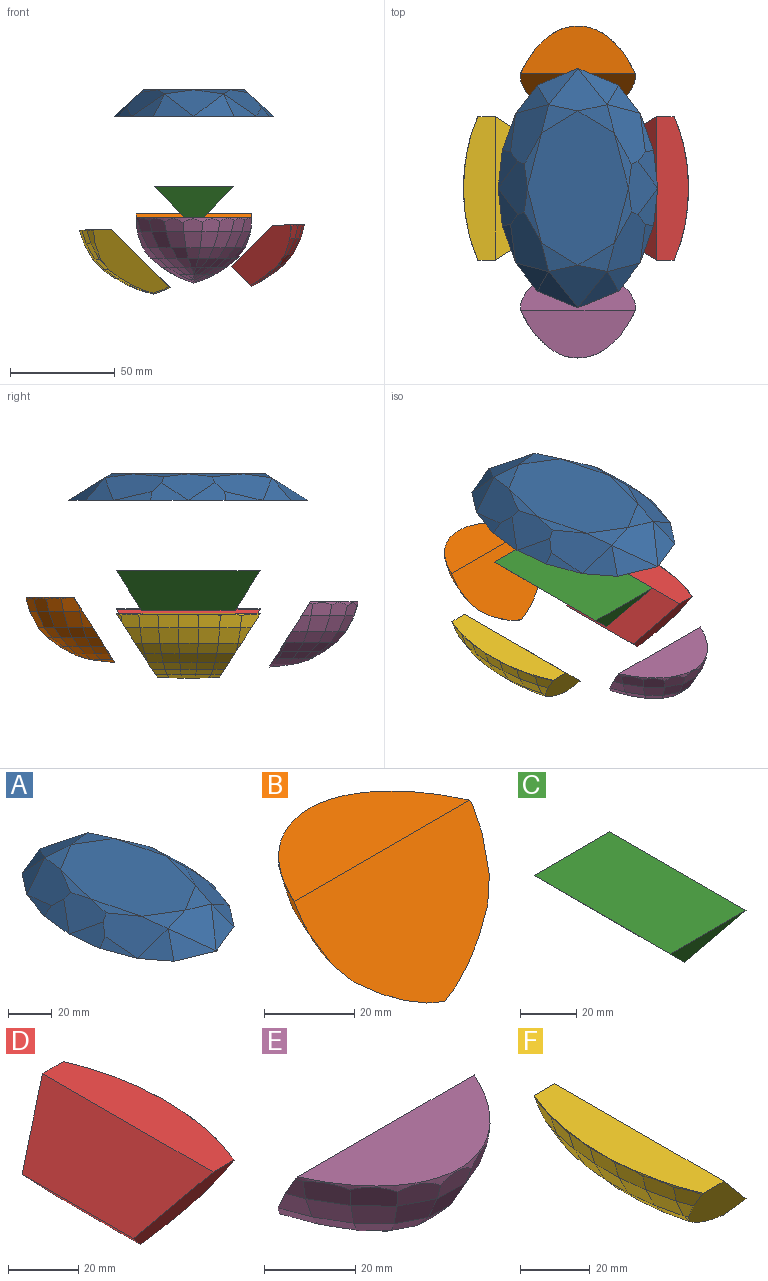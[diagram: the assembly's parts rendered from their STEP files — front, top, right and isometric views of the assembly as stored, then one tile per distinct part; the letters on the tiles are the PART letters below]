
ASSEMBLY  parts=6 mates=5
PART A: 34 faces, bbox 76.2x114.3x12.7 mm
  f0: plane 114.3x76.2mm, normal (0,0,-1), area 6641.7mm2, adj f3,f6,f20,f21,f22,f23,f24,f25
  f1: plane 25.45x13.96mm, normal (-0.67,0,0.74), area 286.1mm2, adj f2,f11,f15,f18,f25,f30
  f2: plane 28.43x18.26mm, normal (-0.59,0.26,0.76), area 396.5mm2, adj f1,f3,f13,f15,f23,f25
  f3: plane 18.41x6.41mm, normal (-0.69,0.25,0.68), area 54.9mm2, adj f0,f2,f25
  f4: plane 25.45x13.96mm, normal (0.67,0,0.74), area 286.1mm2, adj f5,f9,f14,f19,f24,f33
  f5: plane 28.43x18.26mm, normal (0.59,-0.26,0.76), area 396.5mm2, adj f4,f6,f12,f14,f22,f24
  f6: plane 18.41x6.41mm, normal (0.69,-0.25,0.68), area 54.9mm2, adj f0,f5,f24
  f7: plane 73.66x48.26mm, normal (0,0,1), area 2548.9mm2, adj f12,f13,f14,f15,f16,f17,f18,f19
  f8: plane 27.88x20.32mm, normal (0,0.53,0.85), area 334mm2, adj f9,f13,f17,f21,f27,f31
  f9: plane 28.44x18.26mm, normal (0.59,0.26,0.77), area 396.5mm2, adj f4,f8,f17,f19,f31,f32,f33
  f10: plane 27.88x20.32mm, normal (0,-0.53,0.85), area 334mm2, adj f11,f12,f16,f20,f26,f28
  f11: plane 28.44x18.26mm, normal (-0.59,-0.26,0.77), area 396.5mm2, adj f1,f10,f16,f18,f28,f29,f30
  f12: plane 17.43x13.67mm, normal (0.1,-0.16,0.98), area 102.5mm2, adj f5,f7,f10
  f13: plane 17.43x13.67mm, normal (-0.1,0.16,0.98), area 102.5mm2, adj f2,f7,f8
  f14: plane 26.18x8.18mm, normal (0.29,-0.07,0.95), area 60.5mm2, adj f4,f5,f7,f19
  f15: plane 26.18x8.18mm, normal (-0.29,0.07,0.95), area 60.5mm2, adj f1,f2,f7,f18
  f16: plane 17.43x13.67mm, normal (-0.1,-0.16,0.98), area 102.5mm2, adj f7,f10,f11
  f17: plane 17.43x13.67mm, normal (0.1,0.16,0.98), area 102.5mm2, adj f7,f8,f9
  f18: plane 26.23x8.19mm, normal (-0.29,-0.07,0.95), area 60.8mm2, adj f1,f7,f11,f15
  f19: plane 26.23x8.19mm, normal (0.29,0.07,0.95), area 60.8mm2, adj f4,f7,f9,f14
  f20: plane 19.38x17.27mm, normal (0.27,-0.66,0.7), area 159.1mm2, adj f0,f10,f22
  f21: plane 19.38x17.27mm, normal (-0.27,0.66,0.7), area 159.1mm2, adj f0,f8,f23
  f22: plane 15.8x13.48mm, normal (0.58,-0.45,0.68), area 125.1mm2, adj f0,f5,f20
  f23: plane 15.8x13.48mm, normal (-0.58,0.45,0.68), area 125.1mm2, adj f0,f2,f21
  f24: plane 18.03x9.33mm, normal (0.73,-0.08,0.68), area 116.6mm2, adj f0,f4,f5,f6
  f25: plane 18.03x9.33mm, normal (-0.73,0.08,0.68), area 116.6mm2, adj f0,f1,f2,f3
  f26: plane 19.38x17.27mm, normal (-0.27,-0.66,0.7), area 159.1mm2, adj f0,f10,f28
  f27: plane 19.38x17.27mm, normal (0.27,0.66,0.7), area 159.1mm2, adj f0,f8,f31
  f28: plane 15.81x13.48mm, normal (-0.58,-0.45,0.68), area 125.1mm2, adj f0,f10,f11,f26
  f29: plane 18.41x6.41mm, normal (-0.69,-0.25,0.68), area 55.1mm2, adj f0,f11,f30
  f30: plane 18.03x9.37mm, normal (-0.73,-0.08,0.68), area 117.1mm2, adj f0,f1,f11,f29
  f31: plane 15.81x13.48mm, normal (0.58,0.45,0.68), area 125.1mm2, adj f0,f8,f9,f27
  f32: plane 18.41x6.41mm, normal (0.69,0.25,0.68), area 55.1mm2, adj f0,f9,f33
  f33: plane 18.03x9.37mm, normal (0.73,0.08,0.68), area 117.1mm2, adj f0,f4,f9,f32
PART B: 75 faces, bbox 55.2x42.4x31.1 mm
  f0: extruded ~55.11x23.22mm, area 56.9mm2, adj f15,f19,f24,f31,f37,f43,f47,f52
  f1: plane 4.61x1.55mm, normal (-0.29,0.06,-0.96), area 2.4mm2, adj f2,f12,f73,f74
  f2: plane 6.61x4.54mm, normal (-0.28,0.09,-0.96), area 21.6mm2, adj f1,f3,f11,f12,f71
  f3: plane 5.45x2.76mm, normal (-0.27,0.13,-0.96), area 9mm2, adj f2,f5,f11,f30,f66
  f4: plane 7.75x5.71mm, normal (-0.7,0.23,-0.67), area 37.8mm2, adj f6,f68,f69,f74
  f5: plane 1.13x0.58mm, normal (-0.24,0.17,-0.96), area 0.3mm2, adj f3,f30,f61
  f6: plane 8.97x7.42mm, normal (-0.67,0.32,-0.67), area 52mm2, adj f4,f7,f63,f64
  f7: plane 8.62x7.86mm, normal (-0.61,0.43,-0.67), area 49.1mm2, adj f6,f8,f58,f59
  f8: plane 7.99x7.98mm, normal (-0.5,0.55,-0.67), area 45.7mm2, adj f7,f49,f53,f54
  f9: plane 6.35x3.83mm, normal (-0.21,0.47,-0.86), area 13.4mm2, adj f41,f46,f50,f51,f55
  f10: plane 5.82x4.87mm, normal (0.01,0.6,-0.8), area 25.6mm2, adj f40,f45,f46,f50
  f11: plane 7.31x4.22mm, normal (0.28,0.1,-0.96), area 21.2mm2, adj f2,f3,f12,f23,f30
  f12: plane 4.62x2.76mm, normal (0.29,0.06,-0.96), area 7.9mm2, adj f1,f2,f11,f18,f74
  f13: plane 10.5x6.92mm, normal (0.7,0.26,-0.67), area 58.8mm2, adj f14,f20,f21,f26,f74
  f14: plane 0.7x0.61mm, normal (0.72,0.16,-0.67), area 0.1mm2, adj f13,f16,f74
  f15: plane 54.86x22.86mm, normal (0,0,1), area 876.6mm2, adj f0,f74
  f16: plane 5.58x4.27mm, normal (0.58,0.13,-0.8), area 5.7mm2, adj f14,f17,f21,f74
  f17: plane 6.07x3.61mm, normal (0.5,0.11,-0.86), area 11.3mm2, adj f16,f18,f22,f74
  f18: plane 5.8x3.45mm, normal (0.41,0.09,-0.91), area 11.6mm2, adj f12,f17,f23,f74
  f19: plane 6.12x5.39mm, normal (0.9,0.33,-0.29), area 20.7mm2, adj f0,f20,f24,f74
  f20: plane 9.35x7.53mm, normal (0.83,0.31,-0.47), area 55.7mm2, adj f13,f19,f25,f74
  f21: plane 10.21x8.4mm, normal (0.56,0.21,-0.8), area 62.3mm2, adj f13,f16,f22,f27
  f22: plane 9.46x8.34mm, normal (0.48,0.18,-0.86), area 54.7mm2, adj f17,f21,f23,f28
  f23: plane 8.48x7.64mm, normal (0.39,0.15,-0.91), area 42.6mm2, adj f11,f18,f22,f29
  f24: plane 9.87x6.73mm, normal (0.83,0.48,-0.29), area 66.6mm2, adj f0,f19,f25,f31
  f25: plane 10.62x8.4mm, normal (0.76,0.45,-0.47), area 84.4mm2, adj f20,f24,f26,f32
  f26: plane 10.14x8.41mm, normal (0.64,0.37,-0.67), area 60.7mm2, adj f13,f25,f27,f33
  f27: plane 9.89x8.95mm, normal (0.52,0.3,-0.8), area 57.4mm2, adj f21,f26,f28,f34
  f28: plane 9x8.58mm, normal (0.44,0.26,-0.86), area 47.8mm2, adj f22,f27,f29,f35
  f29: plane 7.77x7mm, normal (0.36,0.21,-0.91), area 34.1mm2, adj f23,f28,f30,f36,f61
  f30: plane 4.17x1.97mm, normal (0.26,0.15,-0.96), area 4.2mm2, adj f3,f5,f11,f29
  f31: plane 8.46x8.22mm, normal (0.69,0.66,-0.29), area 63.3mm2, adj f0,f24,f32,f37
  f32: plane 9.7x9.35mm, normal (0.64,0.61,-0.47), area 80.8mm2, adj f25,f31,f33,f38
  f33: plane 9.18x8.87mm, normal (0.54,0.51,-0.67), area 55.5mm2, adj f26,f32,f34,f39
  f34: plane 8.99x8.74mm, normal (0.43,0.41,-0.8), area 48.6mm2, adj f27,f33,f35,f40
  f35: plane 7.96x7.76mm, normal (0.37,0.35,-0.86), area 35.8mm2, adj f28,f34,f36,f41
  f36: plane 5.92x3.93mm, normal (0.3,0.29,-0.91), area 13.6mm2, adj f29,f35,f42,f56,f61
  f37: plane 9.24x6.24mm, normal (0.44,0.85,-0.29), area 57.6mm2, adj f0,f31,f38,f43
  f38: plane 9.36x7.53mm, normal (0.4,0.79,-0.47), area 73.2mm2, adj f32,f37,f39,f44
  f39: plane 8.07x7.2mm, normal (0.34,0.66,-0.67), area 46.3mm2, adj f33,f38,f40,f45
  f40: plane 7.4x6.79mm, normal (0.27,0.53,-0.8), area 34.8mm2, adj f10,f34,f39,f41
  f41: plane 6.57x4.61mm, normal (0.23,0.46,-0.86), area 17.5mm2, adj f9,f35,f40,f42,f46
  f42: plane 1.69x0.99mm, normal (0.19,0.37,-0.91), area 0.9mm2, adj f36,f41,f51,f56
  f43: plane 9.28x6.21mm, normal (0.02,0.96,-0.29), area 53mm2, adj f0,f37,f44,f47
  f44: plane 8.68x7.53mm, normal (0.02,0.88,-0.47), area 66.3mm2, adj f38,f43,f45,f48
  f45: plane 6.89x4.98mm, normal (0.02,0.74,-0.67), area 39.5mm2, adj f10,f39,f44,f49
  f46: plane 5.12x3.06mm, normal (0.01,0.51,-0.86), area 6.8mm2, adj f9,f10,f41
  f47: plane 8.64x6.25mm, normal (-0.38,0.88,-0.29), area 53.1mm2, adj f0,f43,f48,f52
  f48: plane 8.59x7.53mm, normal (-0.35,0.81,-0.47), area 66mm2, adj f44,f47,f49,f53
  f49: plane 7.3x6.63mm, normal (-0.3,0.68,-0.67), area 41.2mm2, adj f8,f45,f48,f50
  f50: plane 7.01x5.97mm, normal (-0.24,0.55,-0.8), area 29.9mm2, adj f9,f10,f49,f54
  f51: plane 0.95x0.5mm, normal (-0.17,0.38,-0.91), area 0.3mm2, adj f9,f42,f56
  f52: plane 7.57x6.98mm, normal (-0.64,0.71,-0.29), area 54.4mm2, adj f0,f47,f53,f57
  f53: plane 8.51x8.36mm, normal (-0.59,0.66,-0.47), area 67.9mm2, adj f8,f48,f52,f58
  f54: plane 7.99x7.76mm, normal (-0.4,0.44,-0.8), area 38.8mm2, adj f8,f50,f55,f59
  f55: plane 7.13x6.75mm, normal (-0.34,0.38,-0.86), area 26.8mm2, adj f9,f54,f56,f60
  f56: plane 4.4x2.8mm, normal (-0.28,0.31,-0.91), area 7.1mm2, adj f36,f42,f51,f55,f61
  f57: plane 8.06x6.43mm, normal (-0.78,0.55,-0.29), area 55.8mm2, adj f0,f52,f58,f62
  f58: plane 8.98x7.92mm, normal (-0.72,0.51,-0.47), area 69.3mm2, adj f7,f53,f57,f63
  f59: plane 8.55x8.3mm, normal (-0.49,0.35,-0.8), area 45.3mm2, adj f7,f54,f60,f64
  f60: plane 7.86x7.78mm, normal (-0.42,0.3,-0.86), area 36.4mm2, adj f55,f59,f61,f65
  f61: plane 6.63x5.49mm, normal (-0.34,0.24,-0.91), area 22.4mm2, adj f5,f29,f36,f56,f60,f66
  f62: plane 8.7x6.49mm, normal (-0.86,0.42,-0.29), area 54.3mm2, adj f0,f57,f63,f67,f74
  f63: plane 9.3x7.53mm, normal (-0.79,0.39,-0.47), area 71.3mm2, adj f6,f58,f62,f68
  f64: plane 8.84x8.2mm, normal (-0.54,0.26,-0.8), area 50.1mm2, adj f6,f59,f65,f69
  f65: plane 8.18x8.06mm, normal (-0.46,0.23,-0.86), area 42.9mm2, adj f60,f64,f66,f70
  f66: plane 7.32x7.23mm, normal (-0.37,0.18,-0.91), area 32.4mm2, adj f3,f61,f65,f71
  f67: plane 2.76x1.73mm, normal (-0.91,0.3,-0.29), area 2.2mm2, adj f62,f68,f74
  f68: plane 7.53x6.14mm, normal (-0.84,0.28,-0.47), area 27.2mm2, adj f4,f63,f67,f74
  f69: plane 8.73x7.35mm, normal (-0.57,0.19,-0.8), area 47.6mm2, adj f4,f64,f70,f74
  f70: plane 8.32x7.76mm, normal (-0.49,0.16,-0.86), area 47.1mm2, adj f65,f69,f71,f72,f74
  f71: plane 7.51x7.21mm, normal (-0.39,0.13,-0.91), area 37.1mm2, adj f2,f66,f70,f73
  f72: plane 4.22x2.62mm, normal (-0.5,0.11,-0.86), area 1.3mm2, adj f70,f73,f74
  f73: plane 5.52x2.56mm, normal (-0.41,0.09,-0.91), area 3.6mm2, adj f1,f71,f72,f74
  f74: plane 55.11x31.07mm, normal (0,-0.85,0.53), area 1502.2mm2, adj f0,f1,f4,f12,f13,f14,f15,f16
PART C: 5 faces, bbox 38.1x68.6x19.1 mm
  f0: plane 68.58x19.05mm, normal (0.71,0,-0.71), area 1525.8mm2, adj f1,f2,f3,f4
  f1: plane 68.58x38.1mm, normal (0,0,1), area 2612.9mm2, adj f0,f2,f3,f4
  f2: plane 38.1x19.05mm, normal (0,0.85,-0.53), area 428.3mm2, adj f0,f1,f4
  f3: plane 38.1x19.05mm, normal (0,-0.85,-0.53), area 428.3mm2, adj f0,f1,f4
  f4: plane 68.58x19.05mm, normal (-0.71,0,-0.71), area 1525.8mm2, adj f0,f1,f2,f3
PART D: 45 faces, bbox 35.5x68.6x28.9 mm
  f0: plane 68.58x20.17mm, normal (-0.69,0,0.73), area 1571.3mm2, adj f2,f3,f43,f44
  f1: extruded ~68.58x6.86mm, area 16.6mm2, adj f2,f5,f6,f17,f24,f28,f32,f34
  f2: plane 68.58x15.24mm, normal (0,0,1), area 895.2mm2, adj f0,f1,f43,f44
  f3: plane 44.69x9.82mm, normal (-0.73,0,-0.69), area 510.5mm2, adj f0,f4,f12,f19,f20,f21,f43,f44
  f4: plane 6.79x3.8mm, normal (0.41,-0.09,-0.91), area 20.6mm2, adj f3,f11,f21,f44
  f5: plane 3.66x2.32mm, normal (0.86,-0.42,-0.29), area 3.5mm2, adj f1,f6,f44
  f6: plane 9.1x6.57mm, normal (0.91,-0.3,-0.29), area 57.8mm2, adj f1,f5,f7,f34,f44
  f7: plane 8.03x7.53mm, normal (0.84,-0.28,-0.47), area 46.2mm2, adj f6,f8,f35,f44
  f8: plane 4.98x4.8mm, normal (0.7,-0.23,-0.67), area 16.5mm2, adj f7,f9,f36,f44
  f9: plane 5.62x4.27mm, normal (0.57,-0.19,-0.8), area 5.9mm2, adj f8,f10,f37,f44
  f10: plane 1.59x0.99mm, normal (0.49,-0.16,-0.86), area 0.2mm2, adj f9,f11,f44
  f11: plane 8.33x7.26mm, normal (0.5,-0.11,-0.86), area 49.4mm2, adj f4,f10,f37,f42,f44
  f12: plane 6.2x3.74mm, normal (0.41,0.09,-0.91), area 18.4mm2, adj f3,f16,f20,f43
  f13: plane 4.28x3.71mm, normal (0.7,0.26,-0.67), area 4.9mm2, adj f14,f18,f43
  f14: plane 10.21x6.39mm, normal (0.72,0.16,-0.67), area 63.1mm2, adj f13,f15,f22,f33,f43
  f15: plane 9.6x7.24mm, normal (0.58,0.13,-0.8), area 57.2mm2, adj f14,f16,f30,f43
  f16: plane 7.9x7.21mm, normal (0.5,0.11,-0.86), area 45.2mm2, adj f12,f15,f31,f43
  f17: plane 8.99x6.5mm, normal (0.9,0.33,-0.29), area 48.4mm2, adj f1,f18,f32,f43
  f18: plane 7.53x6.3mm, normal (0.83,0.31,-0.47), area 30.6mm2, adj f13,f17,f33,f43
  f19: plane 7.59x3.96mm, normal (0.42,0,-0.91), area 32.2mm2, adj f3,f20,f21,f27
  f20: plane 8.03x4.2mm, normal (0.41,0.04,-0.91), area 31.1mm2, adj f3,f12,f19,f31
  f21: plane 7.55x4.18mm, normal (0.41,-0.04,-0.91), area 29.4mm2, adj f3,f4,f19,f42
  f22: plane 9.85x5.46mm, normal (0.74,0.08,-0.67), area 63.2mm2, adj f14,f23,f29,f30
  f23: plane 9.28x4.98mm, normal (0.74,0,-0.67), area 60.7mm2, adj f22,f25,f26,f40
  f24: plane 9.93x6.66mm, normal (0.96,0,-0.29), area 66.5mm2, adj f1,f25,f28,f38
  f25: plane 9.7x7.53mm, normal (0.88,0,-0.47), area 80.8mm2, adj f23,f24,f29,f39
  f26: plane 8.82x5.74mm, normal (0.6,0,-0.8), area 61mm2, adj f23,f27,f30,f41
  f27: plane 8.22x6.01mm, normal (0.51,0,-0.86), area 55.4mm2, adj f19,f26,f31,f42
  f28: plane 10.35x6.64mm, normal (0.95,0.1,-0.29), area 68.9mm2, adj f1,f24,f29,f32
  f29: plane 10.26x7.53mm, normal (0.88,0.09,-0.47), area 84.2mm2, adj f22,f25,f28,f33
  f30: plane 9.42x6.64mm, normal (0.59,0.06,-0.8), area 63.3mm2, adj f15,f22,f26,f31
  f31: plane 8.8x6.84mm, normal (0.51,0.05,-0.86), area 57.5mm2, adj f16,f20,f27,f30
  f32: plane 10.49x6.58mm, normal (0.94,0.21,-0.29), area 68.7mm2, adj f1,f17,f28,f33
  f33: plane 10.61x7.53mm, normal (0.86,0.19,-0.47), area 84.8mm2, adj f14,f18,f29,f32
  f34: plane 9.41x6.63mm, normal (0.94,-0.2,-0.29), area 62.3mm2, adj f1,f6,f35,f38
  f35: plane 9.54x7.53mm, normal (0.87,-0.18,-0.47), area 75.8mm2, adj f7,f34,f36,f39
  f36: plane 9.19x6.13mm, normal (0.73,-0.15,-0.67), area 56.6mm2, adj f8,f35,f37,f40
  f37: plane 8.9x7.24mm, normal (0.58,-0.12,-0.8), area 56.4mm2, adj f9,f11,f36,f41
  f38: plane 9.74x6.67mm, normal (0.95,-0.1,-0.29), area 65.1mm2, adj f1,f24,f34,f39
  f39: plane 9.64x7.53mm, normal (0.88,-0.09,-0.47), area 79mm2, adj f25,f35,f38,f40
  f40: plane 9.26x5.38mm, normal (0.74,-0.08,-0.67), area 59.3mm2, adj f23,f36,f39,f41
  f41: plane 8.86x6.57mm, normal (0.59,-0.06,-0.8), area 59.5mm2, adj f26,f37,f40,f42
  f42: plane 8.28x6.77mm, normal (0.51,-0.05,-0.86), area 54mm2, adj f11,f21,f27,f41
  f43: plane 28.72x28.23mm, normal (0,0.85,-0.53), area 501.3mm2, adj f0,f1,f2,f3,f12,f13,f14,f15
  f44: plane 28.64x28.24mm, normal (0,-0.85,-0.53), area 500.7mm2, adj f0,f1,f2,f3,f4,f5,f6,f7
PART E: 75 faces, bbox 55.2x42.4x31.1 mm
  f0: extruded ~55.11x23.22mm, area 56.9mm2, adj f6,f10,f15,f22,f28,f34,f38,f44
  f1: plane 5.82x4.87mm, normal (-0.01,-0.6,-0.8), area 25.6mm2, adj f31,f36,f37,f41
  f2: plane 7.31x4.22mm, normal (-0.28,-0.1,-0.96), area 21.2mm2, adj f3,f14,f21,f63,f70
  f3: plane 4.62x2.76mm, normal (-0.29,-0.06,-0.96), area 7.9mm2, adj f2,f9,f70,f73,f74
  f4: plane 10.5x6.92mm, normal (-0.7,-0.26,-0.67), area 58.8mm2, adj f5,f11,f12,f17,f74
  f5: plane 0.7x0.61mm, normal (-0.72,-0.16,-0.67), area 0.1mm2, adj f4,f7,f74
  f6: plane 54.86x22.86mm, normal (0,0,1), area 876.6mm2, adj f0,f74
  f7: plane 5.58x4.27mm, normal (-0.58,-0.13,-0.8), area 5.7mm2, adj f5,f8,f12,f74
  f8: plane 6.07x3.61mm, normal (-0.5,-0.11,-0.86), area 11.3mm2, adj f7,f9,f13,f74
  f9: plane 5.8x3.45mm, normal (-0.41,-0.09,-0.91), area 11.6mm2, adj f3,f8,f14,f74
  f10: plane 6.12x5.39mm, normal (-0.9,-0.33,-0.29), area 20.7mm2, adj f0,f11,f15,f74
  f11: plane 9.35x7.53mm, normal (-0.83,-0.31,-0.47), area 55.7mm2, adj f4,f10,f16,f74
  f12: plane 10.21x8.4mm, normal (-0.56,-0.21,-0.8), area 62.3mm2, adj f4,f7,f13,f18
  f13: plane 9.46x8.34mm, normal (-0.48,-0.18,-0.86), area 54.7mm2, adj f8,f12,f14,f19
  f14: plane 8.48x7.64mm, normal (-0.39,-0.15,-0.91), area 42.6mm2, adj f2,f9,f13,f20
  f15: plane 9.87x6.73mm, normal (-0.83,-0.48,-0.29), area 66.6mm2, adj f0,f10,f16,f22
  f16: plane 10.62x8.4mm, normal (-0.76,-0.45,-0.47), area 84.4mm2, adj f11,f15,f17,f23
  f17: plane 10.14x8.41mm, normal (-0.64,-0.37,-0.67), area 60.7mm2, adj f4,f16,f18,f24
  f18: plane 9.89x8.95mm, normal (-0.52,-0.3,-0.8), area 57.4mm2, adj f12,f17,f19,f25
  f19: plane 9x8.58mm, normal (-0.44,-0.26,-0.86), area 47.8mm2, adj f13,f18,f20,f26
  f20: plane 7.77x7mm, normal (-0.36,-0.21,-0.91), area 34.1mm2, adj f14,f19,f21,f27,f55
  f21: plane 4.17x1.97mm, normal (-0.26,-0.15,-0.96), area 4.2mm2, adj f2,f20,f56,f63
  f22: plane 8.46x8.22mm, normal (-0.69,-0.66,-0.29), area 63.3mm2, adj f0,f15,f23,f28
  f23: plane 9.7x9.35mm, normal (-0.64,-0.61,-0.47), area 80.8mm2, adj f16,f22,f24,f29
  f24: plane 9.18x8.87mm, normal (-0.54,-0.51,-0.67), area 55.5mm2, adj f17,f23,f25,f30
  f25: plane 8.99x8.74mm, normal (-0.43,-0.41,-0.8), area 48.6mm2, adj f18,f24,f26,f31
  f26: plane 7.96x7.76mm, normal (-0.37,-0.35,-0.86), area 35.8mm2, adj f19,f25,f27,f32
  f27: plane 5.92x3.93mm, normal (-0.3,-0.29,-0.91), area 13.6mm2, adj f20,f26,f33,f49,f55
  f28: plane 9.24x6.24mm, normal (-0.44,-0.85,-0.29), area 57.6mm2, adj f0,f22,f29,f34
  f29: plane 9.36x7.53mm, normal (-0.4,-0.79,-0.47), area 73.2mm2, adj f23,f28,f30,f35
  f30: plane 8.07x7.2mm, normal (-0.34,-0.66,-0.67), area 46.3mm2, adj f24,f29,f31,f36
  f31: plane 7.4x6.79mm, normal (-0.27,-0.53,-0.8), area 34.8mm2, adj f1,f25,f30,f32
  f32: plane 6.57x4.61mm, normal (-0.23,-0.46,-0.86), area 17.5mm2, adj f26,f31,f33,f37,f42
  f33: plane 1.69x0.99mm, normal (-0.19,-0.37,-0.91), area 0.9mm2, adj f27,f32,f43,f49
  f34: plane 9.28x6.21mm, normal (-0.02,-0.96,-0.29), area 53mm2, adj f0,f28,f35,f38
  f35: plane 8.68x7.53mm, normal (-0.02,-0.88,-0.47), area 66.3mm2, adj f29,f34,f36,f39
  f36: plane 6.89x4.98mm, normal (-0.02,-0.74,-0.67), area 39.5mm2, adj f1,f30,f35,f40
  f37: plane 5.12x3.06mm, normal (-0.01,-0.51,-0.86), area 6.8mm2, adj f1,f32,f42
  f38: plane 8.64x6.25mm, normal (0.38,-0.88,-0.29), area 53.1mm2, adj f0,f34,f39,f44
  f39: plane 8.59x7.53mm, normal (0.35,-0.81,-0.47), area 66mm2, adj f35,f38,f40,f45
  f40: plane 7.3x6.63mm, normal (0.3,-0.68,-0.67), area 41.2mm2, adj f36,f39,f41,f46
  f41: plane 7.01x5.97mm, normal (0.24,-0.55,-0.8), area 29.9mm2, adj f1,f40,f42,f47
  f42: plane 6.35x3.83mm, normal (0.21,-0.47,-0.86), area 13.4mm2, adj f32,f37,f41,f43,f48
  f43: plane 0.95x0.5mm, normal (0.17,-0.38,-0.91), area 0.3mm2, adj f33,f42,f49
  f44: plane 7.57x6.98mm, normal (0.64,-0.71,-0.29), area 54.4mm2, adj f0,f38,f45,f50
  f45: plane 8.51x8.36mm, normal (0.59,-0.66,-0.47), area 67.9mm2, adj f39,f44,f46,f51
  f46: plane 7.99x7.98mm, normal (0.5,-0.55,-0.67), area 45.7mm2, adj f40,f45,f47,f52
  f47: plane 7.99x7.76mm, normal (0.4,-0.44,-0.8), area 38.8mm2, adj f41,f46,f48,f53
  f48: plane 7.13x6.75mm, normal (0.34,-0.38,-0.86), area 26.8mm2, adj f42,f47,f49,f54
  f49: plane 4.4x2.8mm, normal (0.28,-0.31,-0.91), area 7.1mm2, adj f27,f33,f43,f48,f55
  f50: plane 8.06x6.43mm, normal (0.78,-0.55,-0.29), area 55.8mm2, adj f0,f44,f51,f57
  f51: plane 8.98x7.92mm, normal (0.72,-0.51,-0.47), area 69.3mm2, adj f45,f50,f52,f58
  f52: plane 8.62x7.86mm, normal (0.61,-0.43,-0.67), area 49.1mm2, adj f46,f51,f53,f59
  f53: plane 8.55x8.3mm, normal (0.49,-0.35,-0.8), area 45.3mm2, adj f47,f52,f54,f60
  f54: plane 7.86x7.78mm, normal (0.42,-0.3,-0.86), area 36.4mm2, adj f48,f53,f55,f61
  f55: plane 6.63x5.49mm, normal (0.34,-0.24,-0.91), area 22.4mm2, adj f20,f27,f49,f54,f56,f62
  f56: plane 1.13x0.58mm, normal (0.24,-0.17,-0.96), area 0.3mm2, adj f21,f55,f63
  f57: plane 8.7x6.49mm, normal (0.86,-0.42,-0.29), area 54.3mm2, adj f0,f50,f58,f64,f74
  f58: plane 9.3x7.53mm, normal (0.79,-0.39,-0.47), area 71.3mm2, adj f51,f57,f59,f65
  f59: plane 8.97x7.42mm, normal (0.67,-0.32,-0.67), area 52mm2, adj f52,f58,f60,f66
  f60: plane 8.84x8.2mm, normal (0.54,-0.26,-0.8), area 50.1mm2, adj f53,f59,f61,f67
  f61: plane 8.18x8.06mm, normal (0.46,-0.23,-0.86), area 42.9mm2, adj f54,f60,f62,f68
  f62: plane 7.32x7.23mm, normal (0.37,-0.18,-0.91), area 32.4mm2, adj f55,f61,f63,f69
  f63: plane 5.45x2.76mm, normal (0.27,-0.13,-0.96), area 9mm2, adj f2,f21,f56,f62,f70
  f64: plane 2.76x1.73mm, normal (0.91,-0.3,-0.29), area 2.2mm2, adj f57,f65,f74
  f65: plane 7.53x6.14mm, normal (0.84,-0.28,-0.47), area 27.2mm2, adj f58,f64,f66,f74
  f66: plane 7.75x5.71mm, normal (0.7,-0.23,-0.67), area 37.8mm2, adj f59,f65,f67,f74
  f67: plane 8.73x7.35mm, normal (0.57,-0.19,-0.8), area 47.6mm2, adj f60,f66,f68,f74
  f68: plane 8.32x7.76mm, normal (0.49,-0.16,-0.86), area 47.1mm2, adj f61,f67,f69,f71,f74
  f69: plane 7.51x7.21mm, normal (0.39,-0.13,-0.91), area 37.1mm2, adj f62,f68,f70,f72
  f70: plane 6.61x4.54mm, normal (0.28,-0.09,-0.96), area 21.6mm2, adj f2,f3,f63,f69,f73
  f71: plane 4.22x2.62mm, normal (0.5,-0.11,-0.86), area 1.3mm2, adj f68,f72,f74
  f72: plane 5.52x2.56mm, normal (0.41,-0.09,-0.91), area 3.6mm2, adj f69,f71,f73,f74
  f73: plane 4.61x1.55mm, normal (0.29,-0.06,-0.96), area 2.4mm2, adj f3,f70,f72,f74
  f74: plane 55.11x31.07mm, normal (0,0.85,0.53), area 1502.2mm2, adj f0,f3,f4,f5,f6,f7,f8,f9
PART F: 59 faces, bbox 42.5x68.6x31.7 mm
  f0: extruded ~68.58x6.86mm, area 16.6mm2, adj f1,f7,f8,f20,f35,f38,f43,f48
  f1: plane 68.58x15.24mm, normal (0,0,1), area 895.2mm2, adj f0,f2,f57,f58
  f2: plane 68.58x28.87mm, normal (0.73,0,0.69), area 1992.2mm2, adj f1,f6,f22,f33,f34,f55,f57,f58
  f3: plane 6.42x5.81mm, normal (-0.29,0.06,-0.96), area 30.6mm2, adj f5,f13,f27,f31,f58
  f4: plane 4.98x4.8mm, normal (-0.7,0.23,-0.67), area 16.5mm2, adj f9,f10,f30,f58
  f5: plane 5.89x5.73mm, normal (0.29,0.06,-0.96), area 27.3mm2, adj f3,f6,f31,f58
  f6: plane 5.82x3.28mm, normal (0.41,0.09,-0.91), area 15mm2, adj f2,f5,f34,f58
  f7: plane 3.66x2.32mm, normal (-0.86,0.42,-0.29), area 3.5mm2, adj f0,f8,f58
  f8: plane 9.1x6.56mm, normal (-0.91,0.3,-0.29), area 57.8mm2, adj f0,f7,f9,f35,f58
  f9: plane 8.03x7.53mm, normal (-0.84,0.28,-0.47), area 46.2mm2, adj f4,f8,f36,f58
  f10: plane 5.62x4.27mm, normal (-0.57,0.19,-0.8), area 5.9mm2, adj f4,f11,f37,f58
  f11: plane 1.59x0.99mm, normal (-0.49,0.16,-0.86), area 0.2mm2, adj f10,f12,f58
  f12: plane 8.33x7.26mm, normal (-0.5,0.11,-0.86), area 49.4mm2, adj f11,f13,f37,f41,f58
  f13: plane 7.12x6.7mm, normal (-0.41,0.09,-0.91), area 37mm2, adj f3,f12,f42,f58
  f14: plane 5.89x5.73mm, normal (-0.29,-0.06,-0.96), area 27.3mm2, adj f19,f23,f24,f57
  f15: plane 4.28x3.71mm, normal (-0.7,-0.26,-0.67), area 4.9mm2, adj f16,f21,f57
  f16: plane 10.21x6.39mm, normal (-0.72,-0.16,-0.67), area 63.1mm2, adj f15,f17,f26,f54,f57
  f17: plane 9.6x7.24mm, normal (-0.58,-0.13,-0.8), area 57.2mm2, adj f16,f18,f50,f57
  f18: plane 7.9x7.21mm, normal (-0.5,-0.11,-0.86), area 45.2mm2, adj f17,f19,f51,f57
  f19: plane 6.65x6.55mm, normal (-0.41,-0.09,-0.91), area 33.4mm2, adj f14,f18,f52,f57
  f20: plane 8.99x6.5mm, normal (-0.9,-0.33,-0.29), area 48.4mm2, adj f0,f21,f53,f57
  f21: plane 7.53x6.3mm, normal (-0.83,-0.31,-0.47), area 30.6mm2, adj f15,f20,f54,f57
  f22: plane 6.38x3.28mm, normal (0.41,-0.09,-0.91), area 16.5mm2, adj f2,f23,f55,f57
  f23: plane 6.42x5.81mm, normal (0.29,-0.06,-0.96), area 30.6mm2, adj f14,f22,f24,f56,f57
  f24: plane 7.54x6.48mm, normal (-0.29,-0.03,-0.96), area 44.3mm2, adj f14,f23,f25,f52,f56
  f25: plane 7.01x6.48mm, normal (-0.3,0,-0.96), area 45.3mm2, adj f24,f27,f32,f47,f56
  f26: plane 9.85x5.46mm, normal (-0.74,-0.08,-0.67), area 63.2mm2, adj f16,f28,f49,f50
  f27: plane 7.11x6.49mm, normal (-0.29,0.03,-0.96), area 41.9mm2, adj f3,f25,f31,f32,f42
  f28: plane 9.28x4.98mm, normal (-0.74,0,-0.67), area 60.7mm2, adj f26,f29,f44,f45
  f29: plane 9.26x5.38mm, normal (-0.74,0.08,-0.67), area 59.3mm2, adj f28,f30,f39,f40
  f30: plane 9.19x6.13mm, normal (-0.73,0.15,-0.67), area 56.6mm2, adj f4,f29,f36,f37
  f31: plane 7.54x6.48mm, normal (0.29,0.03,-0.96), area 44.3mm2, adj f3,f5,f27,f32,f34
  f32: plane 7.01x6.48mm, normal (0.3,0,-0.96), area 45.3mm2, adj f25,f27,f31,f33,f56
  f33: plane 7.18x1.64mm, normal (0.42,0,-0.91), area 12.8mm2, adj f2,f32,f34,f55
  f34: plane 7.56x2.4mm, normal (0.41,0.04,-0.91), area 15.4mm2, adj f2,f6,f31,f33
  f35: plane 9.4x6.62mm, normal (-0.94,0.2,-0.29), area 62.3mm2, adj f0,f8,f36,f38
  f36: plane 9.54x7.53mm, normal (-0.87,0.18,-0.47), area 75.8mm2, adj f9,f30,f35,f39
  f37: plane 8.9x7.24mm, normal (-0.58,0.12,-0.8), area 56.4mm2, adj f10,f12,f30,f40
  f38: plane 9.73x6.66mm, normal (-0.95,0.1,-0.29), area 65.1mm2, adj f0,f35,f39,f43
  f39: plane 9.64x7.53mm, normal (-0.88,0.09,-0.47), area 79mm2, adj f29,f36,f38,f44
  f40: plane 8.86x6.57mm, normal (-0.59,0.06,-0.8), area 59.5mm2, adj f29,f37,f41,f45
  f41: plane 8.28x6.77mm, normal (-0.51,0.05,-0.86), area 54mm2, adj f12,f40,f42,f46
  f42: plane 7.64x6.3mm, normal (-0.41,0.04,-0.91), area 43.7mm2, adj f13,f27,f41,f47
  f43: plane 9.93x6.66mm, normal (-0.96,0,-0.29), area 66.5mm2, adj f0,f38,f44,f48
  f44: plane 9.7x7.53mm, normal (-0.88,0,-0.47), area 80.8mm2, adj f28,f39,f43,f49
  f45: plane 8.82x5.74mm, normal (-0.6,0,-0.8), area 61mm2, adj f28,f40,f46,f50
  f46: plane 8.22x6.01mm, normal (-0.51,0,-0.86), area 55.4mm2, adj f41,f45,f47,f51
  f47: plane 7.59x5.6mm, normal (-0.42,0,-0.91), area 45mm2, adj f25,f42,f46,f52
  f48: plane 10.35x6.64mm, normal (-0.95,-0.1,-0.29), area 68.9mm2, adj f0,f43,f49,f53
  f49: plane 10.26x7.53mm, normal (-0.88,-0.09,-0.47), area 84.2mm2, adj f26,f44,f48,f54
  f50: plane 9.42x6.64mm, normal (-0.59,-0.06,-0.8), area 63.3mm2, adj f17,f26,f45,f51
  f51: plane 8.8x6.84mm, normal (-0.51,-0.05,-0.86), area 57.5mm2, adj f18,f46,f50,f52
  f52: plane 8.12x6.36mm, normal (-0.41,-0.04,-0.91), area 46.5mm2, adj f19,f24,f47,f51
  f53: plane 10.49x6.58mm, normal (-0.94,-0.21,-0.29), area 68.7mm2, adj f0,f20,f48,f54
  f54: plane 10.61x7.53mm, normal (-0.86,-0.19,-0.47), area 84.8mm2, adj f16,f21,f49,f53
  f55: plane 7.1x2.34mm, normal (0.41,-0.04,-0.91), area 14.3mm2, adj f2,f22,f33,f56
  f56: plane 7.11x6.49mm, normal (0.29,-0.03,-0.96), area 41.9mm2, adj f23,f24,f25,f32,f55
  f57: plane 35.12x31.07mm, normal (0,-0.85,-0.53), area 573.2mm2, adj f0,f1,f2,f14,f15,f16,f17,f18
  f58: plane 35.04x31.07mm, normal (0,0.85,-0.53), area 572.6mm2, adj f0,f1,f2,f3,f4,f5,f6,f7
PLACE A t=(7.33,12.76,54.88)mm
PLACE B t=(7.32,33.13,8.59)mm
PLACE C t=(7.33,12.76,21.36)mm fixed
PLACE D rot(axis=(0,-1,0),1.6deg) t=(25.84,12.76,2.31)mm
PLACE E t=(7.34,-11.15,6.38)mm
PLACE F rot(axis=(0,-1,0),1.7deg) t=(-13.03,12.76,1.59)mm
MATE slider D.f0 <-> C.f0  axis (-0.71,0,0.71) through (35.76,12.76,-6.26)mm
MATE slider C.f2 <-> B.f74  axis (0,0.85,-0.53) through (7.33,43.07,15.01)mm
MATE slider C.f1 <-> A.f0  axis (0,0,1) through (7.33,12.76,21.36)mm
MATE slider C.f3 <-> E.f74  axis (0,-0.85,-0.53) through (7.33,-17.55,15.01)mm
MATE slider C.f4 <-> F.f2  axis (-0.71,0,-0.71) through (-2.86,12.76,12.5)mm
